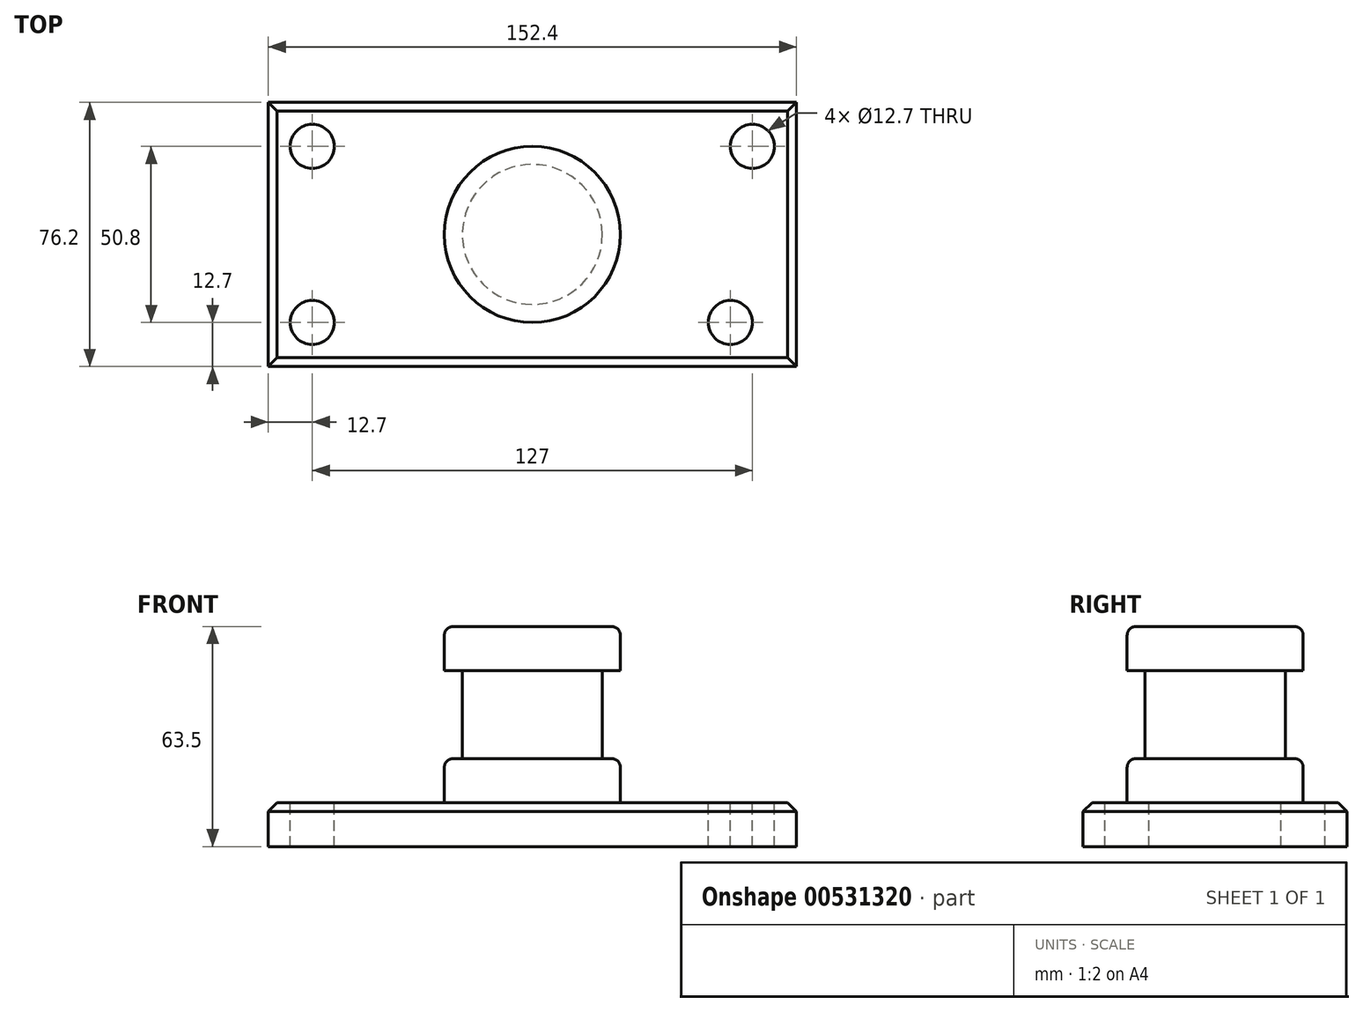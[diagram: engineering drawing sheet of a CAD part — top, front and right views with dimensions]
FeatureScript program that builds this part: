
annotation { "Feature Type Name" : "Feature", "Feature Type Description" : "" }
export const myFeature = defineFeature(function(context is Context, id is Id, definition is map)
    precondition{}
    {
        {
            var Q0;
            Q0=qCreatedBy(makeId("Top.planeOp"),FACE);
            var sketch = newSketch(context, id + "F0", { "sketchPlane" : qUnion([Q0])});
            skLineSegment(sketch, "E0.bottom", {"start": v(76.2, 38.1) * mm, "end": v(-76.2, 38.1) * mm});
            skLineSegment(sketch, "E0.top", {"start": v(76.2, -38.1) * mm, "end": v(-76.2, -38.1) * mm});
            skLineSegment(sketch, "E0.left", {"start": v(76.2, 38.1) * mm, "end": v(76.2, -38.1) * mm});
            skLineSegment(sketch, "E0.right", {"start": v(-76.2, 38.1) * mm, "end": v(-76.2, -38.1) * mm});
            skPoint(sketch, "E0.middle", {"position": v(0, 0) * mm});
            skSolve(sketch);
        }
        {
            var Q0;
            Q0=makeQuery(id+"F0.imprint","IMPRINT",FACE,{"disambiguationData":[TD([[makeQuery(id+"F0.imprint","IMPRINT",EDGE,{"derivedFrom":sQuery(id+"F0.wireOp",EDGE,"E0.bottom")}),1.0]])]});
            extrude(context, id + "F1", {"entities" : qUnion([Q0]), "depth" : 12.7 * mm, "offsetDistance" : 25.4 * mm});
        }
        {
            var Q0;
            Q0=makeQuery(id+"F1.opExtrude","CAP_FACE",FACE,{"disambiguationData":[OSD([sQuery(id+"F0.wireOp",EDGE,"E0.bottom"),sQuery(id+"F0.wireOp",EDGE,"E0.top"),sQuery(id+"F0.wireOp",EDGE,"E0.left"),sQuery(id+"F0.wireOp",EDGE,"E0.right")])],"isStart":false});
            var sketch = newSketch(context, id + "F2", { "sketchPlane" : qUnion([Q0])});
            skCircle(sketch, "E1", {"center": v(-63.5, 25.4) * mm, "radius": 6.35 * mm});
            skCircle(sketch, "E2", {"center": v(57.15, -25.4) * mm, "radius": 6.35 * mm});
            skCircle(sketch, "E3", {"center": v(63.5, 25.4) * mm, "radius": 6.35 * mm});
            skCircle(sketch, "E4", {"center": v(-63.5, -25.4) * mm, "radius": 6.35 * mm});
            skSolve(sketch);
        }
        {
            var Q0;
            Q0=makeQuery(id+"F2.imprint","IMPRINT",FACE,{"disambiguationData":[TD([[makeQuery(id+"F2.imprint","IMPRINT",EDGE,{"derivedFrom":sQuery(id+"F2.wireOp",EDGE,"E2")}),1.0]])]});
            extrude(context, id + "F3", {"entities" : qUnion([Q0]), "operationType" : NewBodyOperationType.REMOVE, "endBound" : BoundingType.THROUGH_ALL, "oppositeDirection" : true, "depth" : 25.4 * mm, "offsetDistance" : 25.4 * mm});
        }
        {
            var Q0;
            Q0=makeQuery(id+"F2.imprint","IMPRINT",FACE,{"disambiguationData":[TD([[makeQuery(id+"F2.imprint","IMPRINT",EDGE,{"derivedFrom":sQuery(id+"F2.wireOp",EDGE,"E3")}),1.0]])]});
            extrude(context, id + "F4", {"entities" : qUnion([Q0]), "operationType" : NewBodyOperationType.REMOVE, "endBound" : BoundingType.THROUGH_ALL, "oppositeDirection" : true, "depth" : 25.4 * mm, "offsetDistance" : 25.4 * mm});
        }
        {
            var Q0;
            Q0=makeQuery(id+"F2.imprint","IMPRINT",FACE,{"disambiguationData":[TD([[makeQuery(id+"F2.imprint","IMPRINT",EDGE,{"derivedFrom":sQuery(id+"F2.wireOp",EDGE,"E4")}),1.0]])]});
            extrude(context, id + "F5", {"entities" : qUnion([Q0]), "operationType" : NewBodyOperationType.REMOVE, "endBound" : BoundingType.THROUGH_ALL, "oppositeDirection" : true, "depth" : 25.4 * mm, "offsetDistance" : 25.4 * mm});
        }
        {
            var Q0;
            Q0=makeQuery(id+"F2.imprint","IMPRINT",FACE,{"disambiguationData":[TD([[makeQuery(id+"F2.imprint","IMPRINT",EDGE,{"derivedFrom":sQuery(id+"F2.wireOp",EDGE,"E1")}),1.0]])]});
            var Q1;
            Q1=sQuery(id+"F2.wireOp",EDGE,"E1");
            extrude(context, id + "F6", {"entities" : qUnion([Q0]), "operationType" : NewBodyOperationType.REMOVE, "surfaceEntities" : qUnion([Q1]), "endBound" : BoundingType.THROUGH_ALL, "oppositeDirection" : true, "depth" : 25.4 * mm, "offsetDistance" : 25.4 * mm});
        }
        {
            var Q0;
            Q0=qCreatedBy(makeId("Front.planeOp"),FACE);
            var sketch = newSketch(context, id + "F7", { "sketchPlane" : qUnion([Q0])});
            skLineSegment(sketch, "E5.bottom", {"start": v(0, 63.5) * mm, "end": v(25.4, 63.5) * mm});
            skLineSegment(sketch, "E5.top", {"start": v(0, 12.7) * mm, "end": v(25.4, 12.7) * mm});
            skLineSegment(sketch, "E5.left", {"start": v(0, 63.5) * mm, "end": v(0, 12.7) * mm});
            skLineSegment(sketch, "E5.right", {"start": v(25.4, 63.5) * mm, "end": v(25.4, 12.7) * mm});
            skSolve(sketch);
        }
        {
            var Q0;
            Q0=makeQuery(id+"F7.imprint","IMPRINT",FACE,{"disambiguationData":[TD([[makeQuery(id+"F7.imprint","IMPRINT",EDGE,{"derivedFrom":sQuery(id+"F7.wireOp",EDGE,"E5.bottom")}),-1.0]])]});
            var Q1;
            Q1=sQuery(id+"F7.wireOp",EDGE,"E5.left");
            revolve(context, id + "F8", {"operationType" : NewBodyOperationType.ADD, "entities" : qUnion([Q0]), "axis" : qUnion([Q1]), "revolveType" : RevolveType.FULL});
        }
        {
            var Q0;
            Q0=qCreatedBy(makeId("Front.planeOp"),FACE);
            var sketch = newSketch(context, id + "F9", { "sketchPlane" : qUnion([Q0])});
            skLineSegment(sketch, "E6.bottom", {"start": v(-30.36, 50.8) * mm, "end": v(-20.2, 50.8) * mm});
            skLineSegment(sketch, "E6.top", {"start": v(-30.36, 25.4) * mm, "end": v(-20.2, 25.4) * mm});
            skLineSegment(sketch, "E6.left", {"start": v(-30.36, 50.8) * mm, "end": v(-30.36, 25.4) * mm});
            skLineSegment(sketch, "E6.right", {"start": v(-20.2, 50.8) * mm, "end": v(-20.2, 25.4) * mm});
            skSolve(sketch);
        }
        {
            var Q0;
            Q0 = qSketchRegion(id + "F9", true);
            var Q1;
            Q1=sQuery(id+"F7.wireOp",EDGE,"E5.left");
            revolve(context, id + "F10", {"operationType" : NewBodyOperationType.REMOVE, "entities" : qUnion([Q0]), "axis" : qUnion([Q1]), "revolveType" : RevolveType.FULL, "oppositeDirection" : true});
        }
        {
            var Q0;
            Q0=makeQuery(id+"F8.opRevolve","SWEPT_EDGE",EDGE,{"disambiguationData":[OSD([sQuery(id+"F7.wireOp",EDGE,"E5.top"),sQuery(id+"F7.wireOp",EDGE,"E5.right")])]});
            var Q1;
            Q1=makeQuery(id+"F10.boolean.opBoolean","INTERSECT",EDGE,{"derivedFrom":[makeQuery(id+"F8.opRevolve","SWEPT_FACE",FACE,{"disambiguationData":[OSD([sQuery(id+"F7.wireOp",EDGE,"E5.right")])]}),makeQuery(id+"F10.opRevolve","SWEPT_FACE",FACE,{"disambiguationData":[OSD([sQuery(id+"F9.wireOp",EDGE,"E6.top")])]})]});
            var Q2;
            Q2=makeQuery(id+"F8.opRevolve","SWEPT_EDGE",EDGE,{"disambiguationData":[OSD([sQuery(id+"F7.wireOp",EDGE,"E5.bottom"),sQuery(id+"F7.wireOp",EDGE,"E5.right")])]});
            fillet(context, id + "F11", {"entities" : qUnion([Q0, Q1, Q2]), "radius" : 2.54 * mm, "tangentPropagation" : true, "allowEdgeOverflow" : false});
        }
        {
            var Q0;
            Q0=makeQuery(id+"F1.opExtrude","CAP_EDGE",EDGE,{"disambiguationData":[OSD([sQuery(id+"F0.wireOp",EDGE,"E0.top")])],"isStart":false});
            var Q1;
            Q1=makeQuery(id+"F1.opExtrude","CAP_EDGE",EDGE,{"disambiguationData":[OSD([sQuery(id+"F0.wireOp",EDGE,"E0.right")])],"isStart":false});
            var Q2;
            Q2=makeQuery(id+"F1.opExtrude","CAP_EDGE",EDGE,{"disambiguationData":[OSD([sQuery(id+"F0.wireOp",EDGE,"E0.bottom")])],"isStart":false});
            var Q3;
            Q3=makeQuery(id+"F1.opExtrude","CAP_EDGE",EDGE,{"disambiguationData":[OSD([sQuery(id+"F0.wireOp",EDGE,"E0.left")])],"isStart":false});
            chamfer(context, id + "F12", {"entities" : qUnion([Q0, Q1, Q2, Q3]), "width" : 2.54 * mm, "tangentPropagation" : true});
        }
    });
